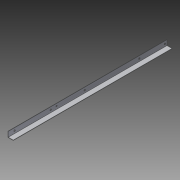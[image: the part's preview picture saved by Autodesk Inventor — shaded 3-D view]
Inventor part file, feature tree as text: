
AUTODESK INVENTOR PART (.ipt)
format: ipt  version: 2014 SP1 (Build 180222100, 222)  size: 93,696 bytes
history: native  units: in
note: dims shown in document units (in); Inventor stores cm internally (conversion verified against a paired STEP export)
features: extrude x2, sketch x2, reference x2
ambient origin geometry x8: Origin, YZ Plane, XZ Plane, XY Plane, X Axis, Y Axis, Z Axis, Center Point
bodies: Solid1 (feature_tree)
feature tree (6):
  extrude  "Extrusion1"  Depth=0.0312in
  extrude  "Extrusion2"  Depth=18.688in TaperAngle=0.0deg
  sketch  "Sketch1"  dims[d0=0.625in d1=0.0312in]
  sketch  "Sketch2"  dims[d2=0.0312in d3=18.688in d4=0.0in d5=1.0in d6=0.0in]
  reference  "Reference2"
  reference  "Reference3"
